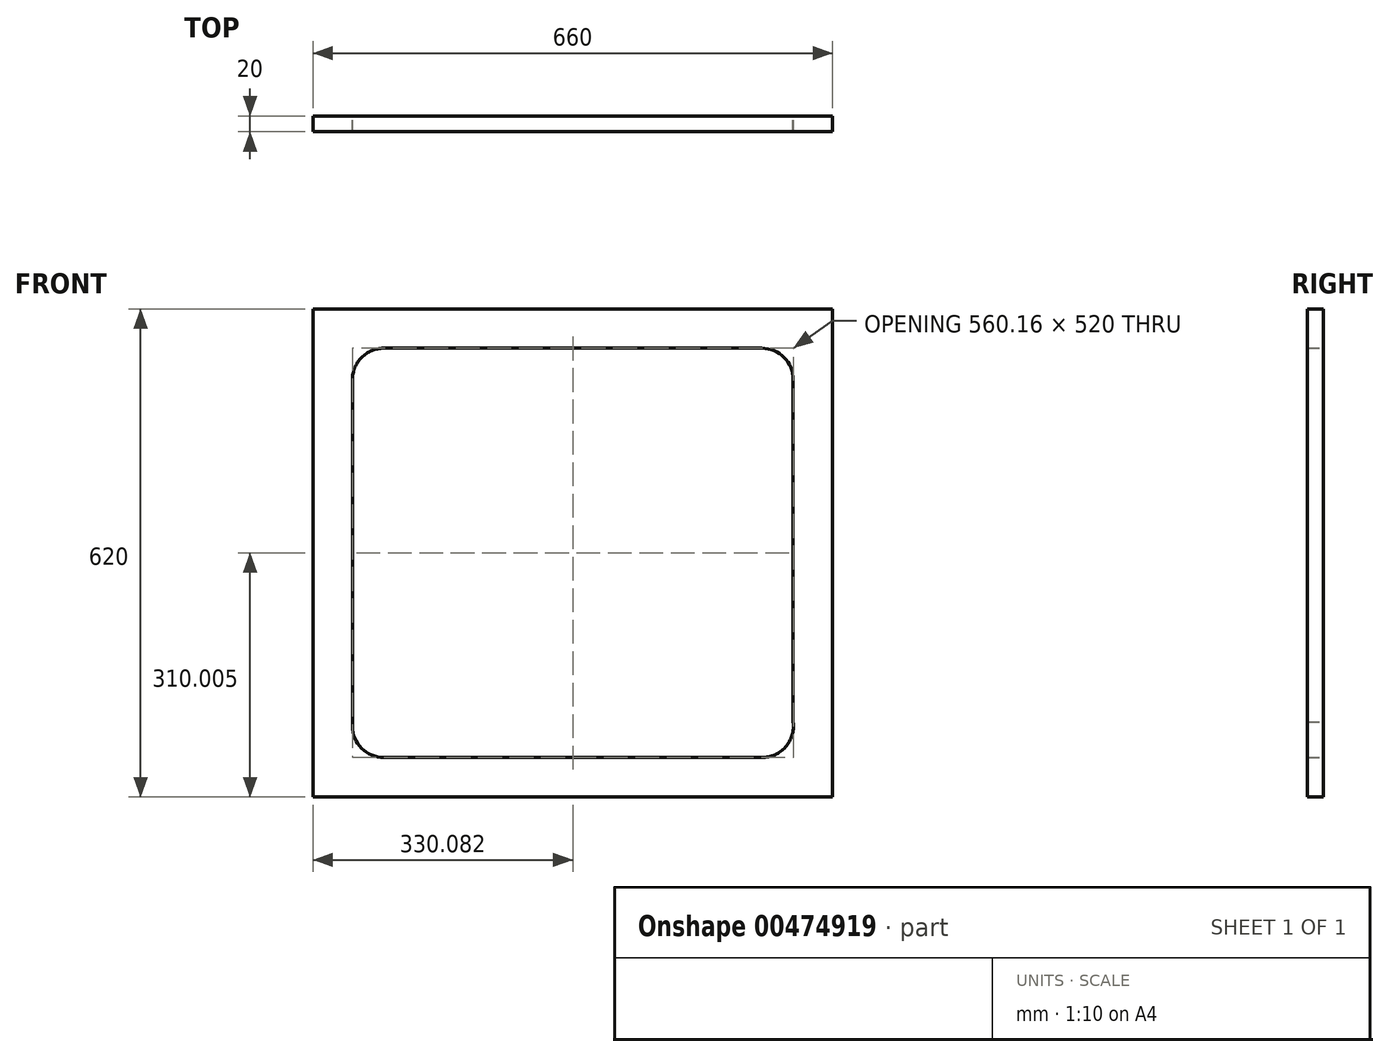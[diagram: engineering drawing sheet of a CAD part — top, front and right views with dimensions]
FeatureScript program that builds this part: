
annotation { "Feature Type Name" : "Feature", "Feature Type Description" : "" }
export const myFeature = defineFeature(function(context is Context, id is Id, definition is map)
    precondition{}
    {
        {
            var Q0;
            Q0=qCreatedBy(makeId("Front.planeOp"),FACE);
            var sketch = newSketch(context, id + "F0", { "sketchPlane" : qUnion([Q0])});
            skLineSegment(sketch, "E0.top", {"start": v(-279.26, -229.92) * mm, "end": v(380.74, -229.92) * mm});
            skArc(sketch, "E1", {"start": v(-189.26, 340.08) * mm, "mid": v(-217.54, 328.37) * mm, "end": v(-229.26, 300.08) * mm});
            skPoint(sketch, "E2.orphan", {"position": v(-229.26, 340.08) * mm});
            skArc(sketch, "E3.MirrorCS", {"start": v(290.74, 340.08) * mm, "mid": v(319.03, 328.37) * mm, "end": v(330.74, 300.08) * mm});
            skArc(sketch, "E4.MirrorCS", {"start": v(290.74, -179.92) * mm, "mid": v(320.95, -166.5) * mm, "end": v(330.74, -134.92) * mm});
            skArc(sketch, "E5.MirrorCS", {"start": v(-189.26, -179.92) * mm, "mid": v(-217.54, -168.2) * mm, "end": v(-229.26, -139.92) * mm});
            skLineSegment(sketch, "E6", {"start": v(-279.26, 390.08) * mm, "end": v(380.74, 390.08) * mm});
            skLineSegment(sketch, "E7", {"start": v(-279.26, 390.08) * mm, "end": v(-279.26, -229.92) * mm});
            skLineSegment(sketch, "E8", {"start": v(380.74, 390.08) * mm, "end": v(380.74, -229.92) * mm});
            skLineSegment(sketch, "E9", {"start": v(-189.26, 340.08) * mm, "end": v(290.74, 340.08) * mm});
            skLineSegment(sketch, "E10", {"start": v(-229.26, 300.08) * mm, "end": v(-229.26, -139.92) * mm});
            skLineSegment(sketch, "E11", {"start": v(-189.26, -179.92) * mm, "end": v(290.74, -179.92) * mm});
            skLineSegment(sketch, "E12", {"start": v(330.74, -134.92) * mm, "end": v(330.74, 300.08) * mm});
            skSolve(sketch);
        }
        {
            var Q0;
            Q0=makeQuery(id+"F0.imprint","IMPRINT",FACE,{"disambiguationData":[TD([[makeQuery(id+"F0.imprint","IMPRINT",EDGE,{"derivedFrom":sQuery(id+"F0.wireOp",EDGE,"E0.bottom")}),-1.0]])]});
            var Q1;
            Q1=makeQuery(id+"F0.imprint","IMPRINT",FACE,{"disambiguationData":[TD([[makeQuery(id+"F0.imprint","IMPRINT",EDGE,{"derivedFrom":sQuery(id+"F0.wireOp",EDGE,"E0.top")}),1.0]])]});
            extrude(context, id + "F1", {"entities" : qUnion([Q0, Q1]), "depth" : 20 * mm, "offsetDistance" : 25 * mm});
        }
    });
